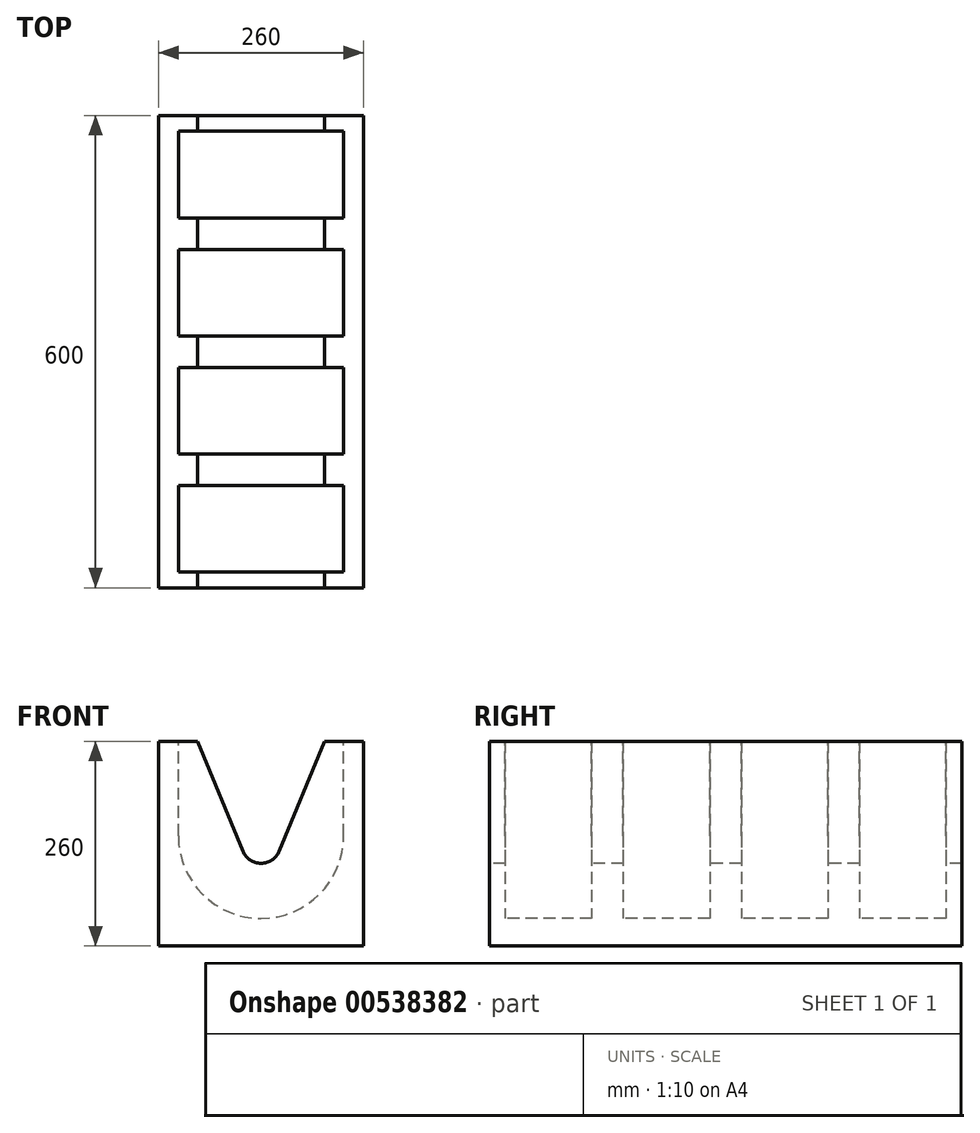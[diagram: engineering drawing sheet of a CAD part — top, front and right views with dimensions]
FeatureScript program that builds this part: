
annotation { "Feature Type Name" : "Feature", "Feature Type Description" : "" }
export const myFeature = defineFeature(function(context is Context, id is Id, definition is map)
    precondition{}
    {
        {
            var Q0;
            Q0=qCreatedBy(makeId("Top.planeOp"),FACE);
            var sketch = newSketch(context, id + "F0", { "sketchPlane" : qUnion([Q0])});
            skLineSegment(sketch, "E0", {"start": v(0, 0) * mm, "end": v(130, 0) * mm});
            skLineSegment(sketch, "E1", {"start": v(130, 0) * mm, "end": v(130, 600) * mm});
            skLineSegment(sketch, "E2", {"start": v(130, 600) * mm, "end": v(-130, 600) * mm});
            skLineSegment(sketch, "E3", {"start": v(-130, 600) * mm, "end": v(-130, 0) * mm});
            skLineSegment(sketch, "E4", {"start": v(-130, 0) * mm, "end": v(0, 0) * mm});
            skSolve(sketch);
        }
        {
            var Q0;
            Q0 = qSketchRegion(id + "F0", true);
            extrude(context, id + "F1", {"entities" : qUnion([Q0]), "depth" : 260 * mm, "offsetDistance" : 25 * mm});
        }
        {
            var Q0;
            Q0=makeQuery(id+"F1.opExtrude","CAP_FACE",FACE,{"disambiguationData":[OSD([sQuery(id+"F0.wireOp",EDGE,"E0"),sQuery(id+"F0.wireOp",EDGE,"E1"),sQuery(id+"F0.wireOp",EDGE,"E2"),sQuery(id+"F0.wireOp",EDGE,"E3"),sQuery(id+"F0.wireOp",EDGE,"E4")])],"isStart":false});
            var sketch = newSketch(context, id + "F2", { "sketchPlane" : qUnion([Q0])});
            skLineSegment(sketch, "E5.bottom", {"start": v(-105, 580) * mm, "end": v(105, 580) * mm});
            skLineSegment(sketch, "E5.top", {"start": v(-105, 470) * mm, "end": v(105, 470) * mm});
            skLineSegment(sketch, "E5.left", {"start": v(-105, 580) * mm, "end": v(-105, 470) * mm});
            skLineSegment(sketch, "E5.right", {"start": v(105, 580) * mm, "end": v(105, 470) * mm});
            skLineSegment(sketch, "E6.bottom", {"start": v(-105, 280) * mm, "end": v(105, 280) * mm});
            skLineSegment(sketch, "E6.top", {"start": v(-105, 170) * mm, "end": v(105, 170) * mm});
            skLineSegment(sketch, "E6.left", {"start": v(-105, 280) * mm, "end": v(-105, 170) * mm});
            skLineSegment(sketch, "E6.right", {"start": v(105, 280) * mm, "end": v(105, 170) * mm});
            skLineSegment(sketch, "E7.bottom", {"start": v(-105, 430) * mm, "end": v(105, 430) * mm});
            skLineSegment(sketch, "E7.top", {"start": v(-105, 320) * mm, "end": v(105, 320) * mm});
            skLineSegment(sketch, "E7.left", {"start": v(-105, 430) * mm, "end": v(-105, 320) * mm});
            skLineSegment(sketch, "E7.right", {"start": v(105, 430) * mm, "end": v(105, 320) * mm});
            skLineSegment(sketch, "E8.bottom", {"start": v(-105, 130) * mm, "end": v(105, 130) * mm});
            skLineSegment(sketch, "E8.top", {"start": v(-105, 20) * mm, "end": v(105, 20) * mm});
            skLineSegment(sketch, "E8.left", {"start": v(-105, 130) * mm, "end": v(-105, 20) * mm});
            skLineSegment(sketch, "E8.right", {"start": v(105, 130) * mm, "end": v(105, 20) * mm});
            skSolve(sketch);
        }
        {
            var Q0;
            Q0 = qSketchRegion(id + "F2", true);
            extrude(context, id + "F3", {"entities" : qUnion([Q0]), "operationType" : NewBodyOperationType.REMOVE, "oppositeDirection" : true, "depth" : 225 * mm, "offsetDistance" : 25 * mm});
        }
        {
            var Q0;
            Q0=makeQuery(id+"F3.boolean.opBoolean","COPY",EDGE,{"derivedFrom":makeQuery(id+"F3.opExtrude","CAP_EDGE",EDGE,{"disambiguationData":[OSD([sQuery(id+"F2.wireOp",EDGE,"E8.left")])],"isStart":false})});
            var Q1;
            Q1=makeQuery(id+"F3.boolean.opBoolean","COPY",EDGE,{"derivedFrom":makeQuery(id+"F3.opExtrude","CAP_EDGE",EDGE,{"disambiguationData":[OSD([sQuery(id+"F2.wireOp",EDGE,"E8.right")])],"isStart":false})});
            var Q2;
            Q2=makeQuery(id+"F3.boolean.opBoolean","COPY",EDGE,{"derivedFrom":makeQuery(id+"F3.opExtrude","CAP_EDGE",EDGE,{"disambiguationData":[OSD([sQuery(id+"F2.wireOp",EDGE,"E6.left")])],"isStart":false})});
            var Q3;
            Q3=makeQuery(id+"F3.boolean.opBoolean","COPY",EDGE,{"derivedFrom":makeQuery(id+"F3.opExtrude","CAP_EDGE",EDGE,{"disambiguationData":[OSD([sQuery(id+"F2.wireOp",EDGE,"E7.left")])],"isStart":false})});
            var Q4;
            Q4=makeQuery(id+"F3.boolean.opBoolean","COPY",EDGE,{"derivedFrom":makeQuery(id+"F3.opExtrude","CAP_EDGE",EDGE,{"disambiguationData":[OSD([sQuery(id+"F2.wireOp",EDGE,"E5.left")])],"isStart":false})});
            var Q5;
            Q5=makeQuery(id+"F3.boolean.opBoolean","COPY",EDGE,{"derivedFrom":makeQuery(id+"F3.opExtrude","CAP_EDGE",EDGE,{"disambiguationData":[OSD([sQuery(id+"F2.wireOp",EDGE,"E6.right")])],"isStart":false})});
            var Q6;
            Q6=makeQuery(id+"F3.boolean.opBoolean","COPY",EDGE,{"derivedFrom":makeQuery(id+"F3.opExtrude","CAP_EDGE",EDGE,{"disambiguationData":[OSD([sQuery(id+"F2.wireOp",EDGE,"E7.right")])],"isStart":false})});
            var Q7;
            Q7=makeQuery(id+"F3.boolean.opBoolean","COPY",EDGE,{"derivedFrom":makeQuery(id+"F3.opExtrude","CAP_EDGE",EDGE,{"disambiguationData":[OSD([sQuery(id+"F2.wireOp",EDGE,"E5.right")])],"isStart":false})});
            fillet(context, id + "F4", {"entities" : qUnion([Q0, Q1, Q2, Q3, Q4, Q5, Q6, Q7]), "radius" : 105 * mm, "tangentPropagation" : true, "allowEdgeOverflow" : false});
        }
        {
            var Q0;
            Q0=makeQuery(id+"F1.opExtrude","SWEPT_FACE",FACE,{"disambiguationData":[OSD([sQuery(id+"F0.wireOp",EDGE,"E0"),sQuery(id+"F0.wireOp",EDGE,"E4")])]});
            var sketch = newSketch(context, id + "F5", { "sketchPlane" : qUnion([Q0])});
            skLineSegment(sketch, "E9", {"start": v(0, 0) * mm, "end": v(0, 260) * mm, "construction": true});
            skCircle(sketch, "E10", {"center": v(0, 130) * mm, "radius": 25 * mm});
            skLineSegment(sketch, "E11", {"start": v(80.9, 260) * mm, "end": v(23.1, 120.43) * mm});
            skLineSegment(sketch, "E12", {"start": v(-80.9, 260) * mm, "end": v(-23.1, 120.43) * mm});
            skLineSegment(sketch, "E13", {"start": v(-80.9, 260) * mm, "end": v(0, 260) * mm});
            skLineSegment(sketch, "E14", {"start": v(0, 260) * mm, "end": v(80.9, 260) * mm});
            skSolve(sketch);
        }
        {
            var Q0;
            Q0 = qSketchRegion(id + "F5", true);
            extrude(context, id + "F6", {"entities" : qUnion([Q0]), "operationType" : NewBodyOperationType.REMOVE, "endBound" : BoundingType.THROUGH_ALL, "oppositeDirection" : true, "depth" : 25 * mm, "offsetDistance" : 25 * mm});
        }
    });
